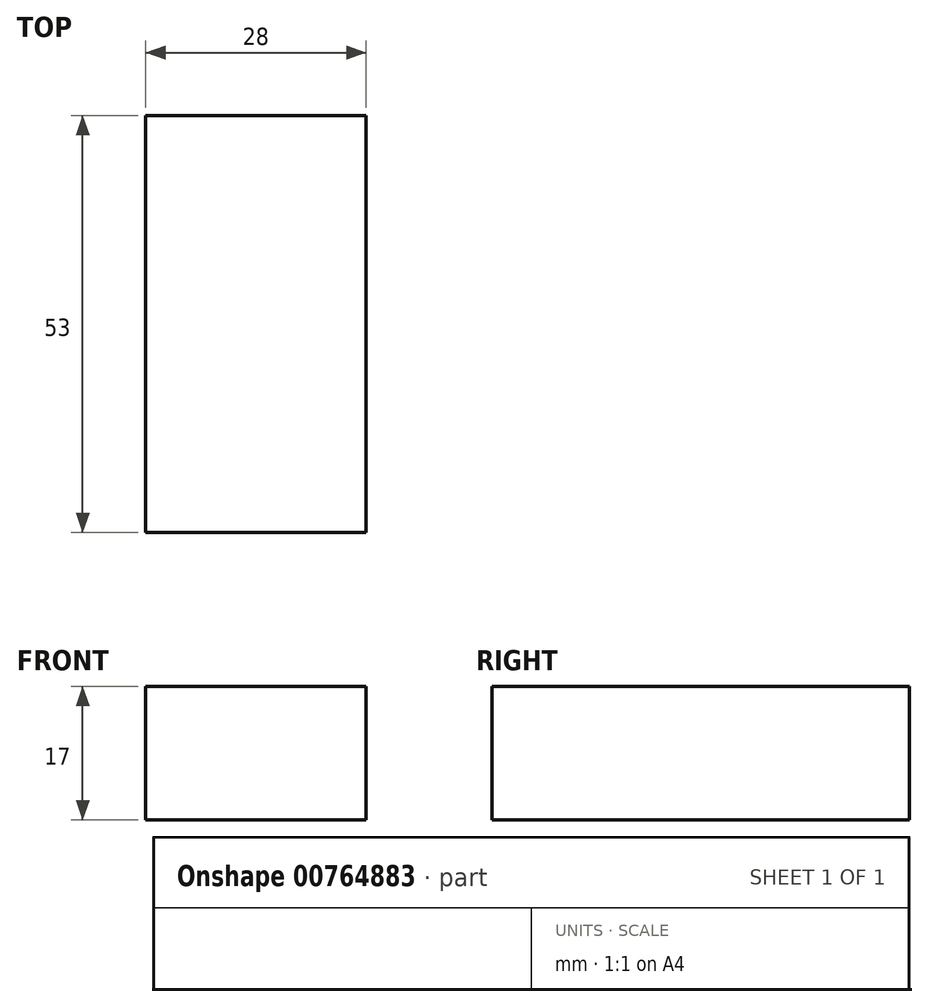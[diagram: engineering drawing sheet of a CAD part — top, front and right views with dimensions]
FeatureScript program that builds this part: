
annotation { "Feature Type Name" : "Feature", "Feature Type Description" : "" }
export const myFeature = defineFeature(function(context is Context, id is Id, definition is map)
    precondition{}
    {
        {
            var Q0;
            Q0=qCreatedBy(makeId("Front.planeOp"),FACE);
            var sketch = newSketch(context, id + "F0", { "sketchPlane" : qUnion([Q0])});
            skLineSegment(sketch, "E0.bottom", {"start": v(0, 0) * mm, "end": v(28, 0) * mm});
            skLineSegment(sketch, "E0.top", {"start": v(0, 17) * mm, "end": v(28, 17) * mm});
            skLineSegment(sketch, "E0.left", {"start": v(0, 0) * mm, "end": v(0, 17) * mm});
            skLineSegment(sketch, "E0.right", {"start": v(28, 0) * mm, "end": v(28, 17) * mm});
            skSolve(sketch);
        }
        {
            var Q0;
            Q0=makeQuery(id+"F0.imprint","IMPRINT",FACE,{"disambiguationData":[TD([[makeQuery(id+"F0.imprint","IMPRINT",EDGE,{"derivedFrom":sQuery(id+"F0.wireOp",EDGE,"E0.bottom")}),1.0]])]});
            extrude(context, id + "F1", {"entities" : qUnion([Q0]), "depth" : 53 * mm, "offsetDistance" : 25 * mm});
        }
    });
